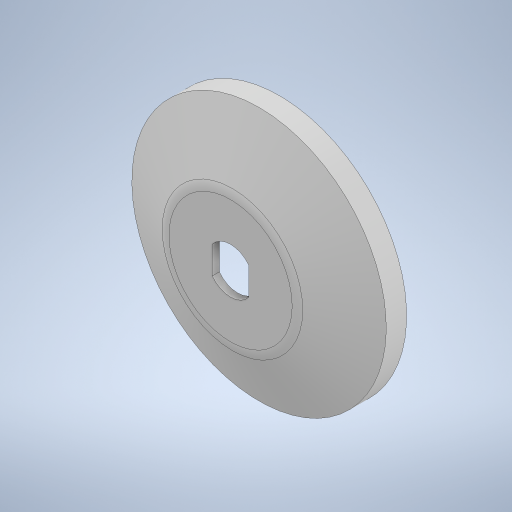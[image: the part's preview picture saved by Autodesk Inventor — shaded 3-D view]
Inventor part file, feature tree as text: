
AUTODESK INVENTOR PART (.ipt)
format: ipt  version: 2023 (Build 270158000, 158)  size: 366,080 bytes
history: native  units: mm
features: sketch x6, extrude x5, revolve x1, fillet x1, plane x1, pattern_circular x1, mirror x1
ambient origin geometry x8: Origin, YZ Plane, XZ Plane, XY Plane, X Axis, Y Axis, Z Axis, Center Point
bodies: Solid1 (feature_tree)
feature tree (16):
  extrude  "Extrusion1"  Depth=18.0mm
  revolve  "Revolution1"  [1 undecoded]
  fillet  "Fillet1"  Radius=7.0mm
  plane  "Work Plane2"
  extrude  "Extrusion2"  Depth=11.0mm
  sketch  "Sketch4"  dims[d11=30.0mm d12=90.0deg]
  extrude  "Extrusion3"  TaperAngle=90.0deg  [1 undecoded]
  pattern_circular  "Circular Pattern1"  [2 undecoded]
  mirror  "Mirror1"
  extrude  "Extrusion4"  Depth=10.0mm
  extrude  "Extrusion5"  TaperAngle=0.0deg  [1 undecoded]
  sketch  "Sketch1"  dims[d0=22.5mm d1=18.0mm]
  sketch  "Sketch2"  dims[d2=65.0mm d3=3.5mm d4=0.0mm d8=7.0mm]
  sketch  "Sketch3"  dims[d9=25.0mm d10=11.0mm]
  sketch  "Sketch5"  dims[d13=10.0mm]
  sketch  "Sketch6"  dims[d14=9.0mm d19=61.0mm d20=6.0mm d21=0.0mm d22=1.0mm d23=0.0mm d24=0.0mm d25=45.0mm d26=18.0mm d27=100.0mm d28=360.0deg d30=1.0mm d31=0.0mm d32=2.0mm d33=2.5mm d34=10.0mm d35=0.0mm]
note: 5 required parameter values undecoded (feature->parameter linkage not recoverable at this tier; creation-order binding heuristic only, values carry confidence <= 0.55)